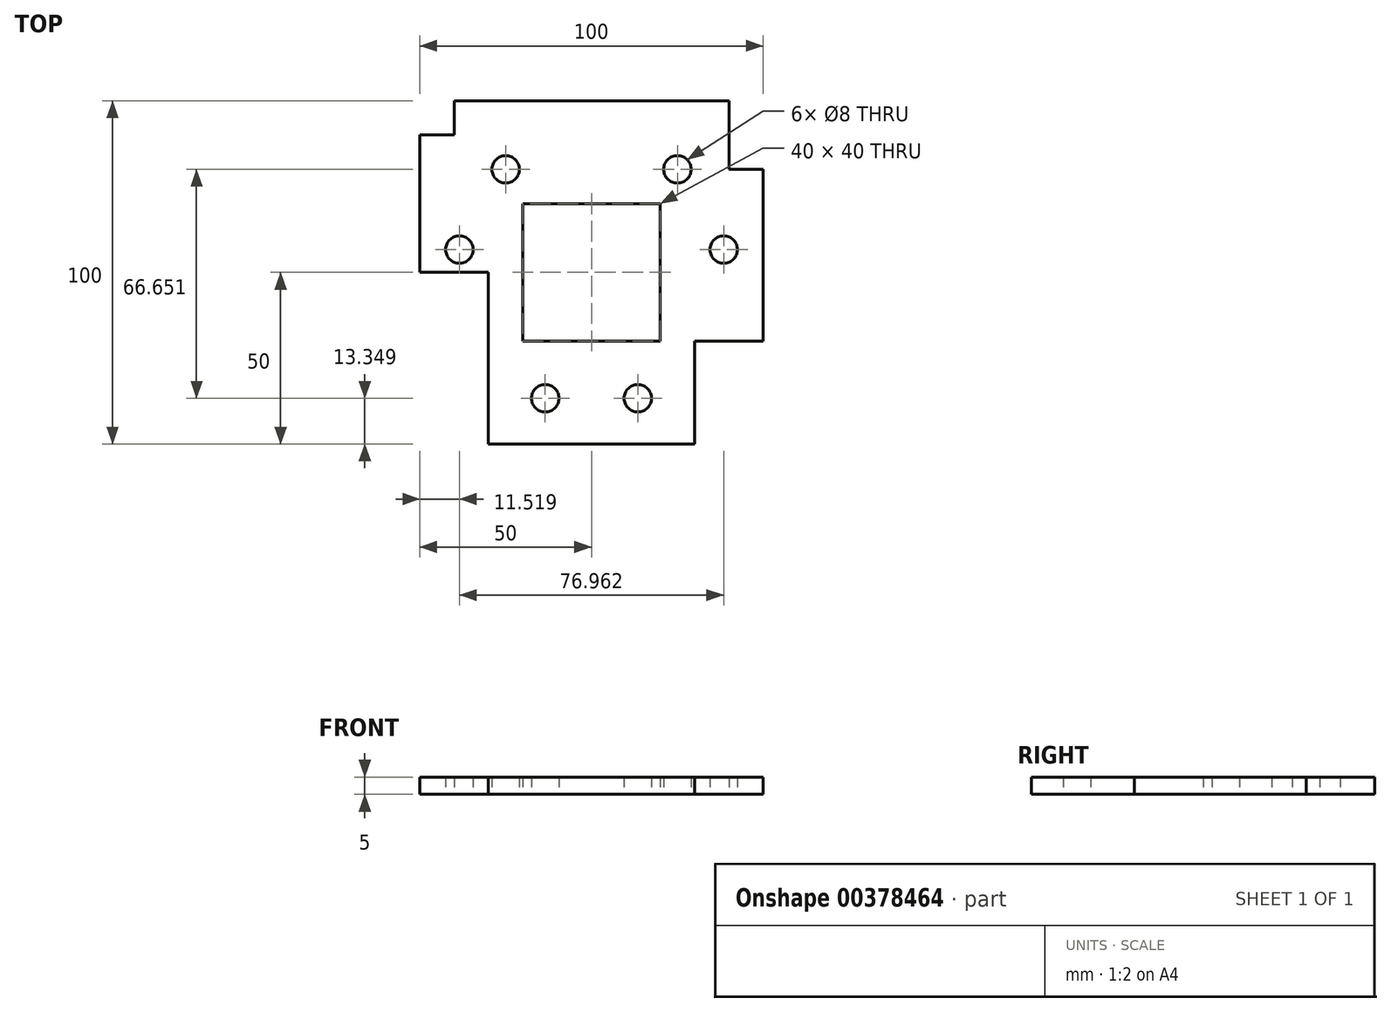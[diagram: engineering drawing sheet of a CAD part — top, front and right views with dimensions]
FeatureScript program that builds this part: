
annotation { "Feature Type Name" : "Feature", "Feature Type Description" : "" }
export const myFeature = defineFeature(function(context is Context, id is Id, definition is map)
    precondition{}
    {
        {
            var Q0;
            Q0=qCreatedBy(makeId("Top.planeOp"),FACE);
            var sketch = newSketch(context, id + "F0", { "sketchPlane" : qUnion([Q0])});
            skCircle(sketch, "E0", {"center": v(-25, 30) * mm, "radius": 4 * mm});
            skCircle(sketch, "E1", {"center": v(25, 30) * mm, "radius": 4 * mm});
            skLineSegment(sketch, "E2", {"start": v(-25, 30) * mm, "end": v(25, 30) * mm, "construction": true});
            skPoint(sketch, "E3", {"position": v(0, 30) * mm});
            skLineSegment(sketch, "E4", {"start": v(0, 30) * mm, "end": v(0, 0) * mm, "construction": true});
            skCircle(sketch, "E5.1.0", {"center": v(-13.48, -36.65) * mm, "radius": 4 * mm});
            skCircle(sketch, "E5.1.1", {"center": v(-38.48, 6.65) * mm, "radius": 4 * mm});
            skCircle(sketch, "E5.2.0", {"center": v(38.48, 6.65) * mm, "radius": 4 * mm});
            skCircle(sketch, "E5.2.1", {"center": v(13.48, -36.65) * mm, "radius": 4 * mm});
            skPoint(sketch, "E5.center", {"position": v(0, 0) * mm});
            skLineSegment(sketch, "E6.bottom", {"start": v(-50, 50) * mm, "end": v(50, 50) * mm});
            skLineSegment(sketch, "E6.top", {"start": v(-50, -50) * mm, "end": v(50, -50) * mm});
            skLineSegment(sketch, "E6.left", {"start": v(-50, 50) * mm, "end": v(-50, -50) * mm});
            skLineSegment(sketch, "E6.right", {"start": v(50, 50) * mm, "end": v(50, -50) * mm});
            skLineSegment(sketch, "E7", {"start": v(0, 50) * mm, "end": v(0, 0) * mm, "construction": true});
            skLineSegment(sketch, "E8", {"start": v(-50, 0) * mm, "end": v(0, 0) * mm, "construction": true});
            skLineSegment(sketch, "E9.bottom", {"start": v(20, 20) * mm, "end": v(-20, 20) * mm});
            skLineSegment(sketch, "E9.top", {"start": v(20, -20) * mm, "end": v(-20, -20) * mm});
            skLineSegment(sketch, "E9.left", {"start": v(20, 20) * mm, "end": v(20, -20) * mm});
            skLineSegment(sketch, "E9.right", {"start": v(-20, 20) * mm, "end": v(-20, -20) * mm});
            skLineSegment(sketch, "E10.bottom", {"start": v(-50, 50) * mm, "end": v(-40, 50) * mm});
            skLineSegment(sketch, "E10.top", {"start": v(-50, 40) * mm, "end": v(-40, 40) * mm});
            skLineSegment(sketch, "E10.left", {"start": v(-50, 50) * mm, "end": v(-50, 40) * mm});
            skLineSegment(sketch, "E10.right", {"start": v(-40, 50) * mm, "end": v(-40, 40) * mm});
            skLineSegment(sketch, "E11.bottom", {"start": v(50, 50) * mm, "end": v(40, 50) * mm});
            skLineSegment(sketch, "E11.top", {"start": v(50, 30) * mm, "end": v(40, 30) * mm});
            skLineSegment(sketch, "E11.left", {"start": v(50, 50) * mm, "end": v(50, 30) * mm});
            skLineSegment(sketch, "E11.right", {"start": v(40, 50) * mm, "end": v(40, 30) * mm});
            skLineSegment(sketch, "E12.bottom", {"start": v(50, -50) * mm, "end": v(30, -50) * mm});
            skLineSegment(sketch, "E12.top", {"start": v(50, -20) * mm, "end": v(30, -20) * mm});
            skLineSegment(sketch, "E12.left", {"start": v(50, -50) * mm, "end": v(50, -20) * mm});
            skLineSegment(sketch, "E12.right", {"start": v(30, -50) * mm, "end": v(30, -20) * mm});
            skLineSegment(sketch, "E13.bottom", {"start": v(-50, -50) * mm, "end": v(-30, -50) * mm});
            skLineSegment(sketch, "E13.top", {"start": v(-50, 0) * mm, "end": v(-30, 0) * mm});
            skLineSegment(sketch, "E13.left", {"start": v(-50, -50) * mm, "end": v(-50, 0) * mm});
            skLineSegment(sketch, "E13.right", {"start": v(-30, -50) * mm, "end": v(-30, 0) * mm});
            skSolve(sketch);
        }
        {
            var Q0;
            Q0=makeQuery(id+"F0.imprint","IMPRINT",FACE,{"disambiguationData":[TD([[makeQuery(id+"F0.imprint","IMPRINT",EDGE,{"derivedFrom":sQuery(id+"F0.wireOp",EDGE,"E0")}),-1.0]])]});
            extrude(context, id + "F1", {"entities" : qUnion([Q0]), "depth" : 5 * mm});
        }
    });
